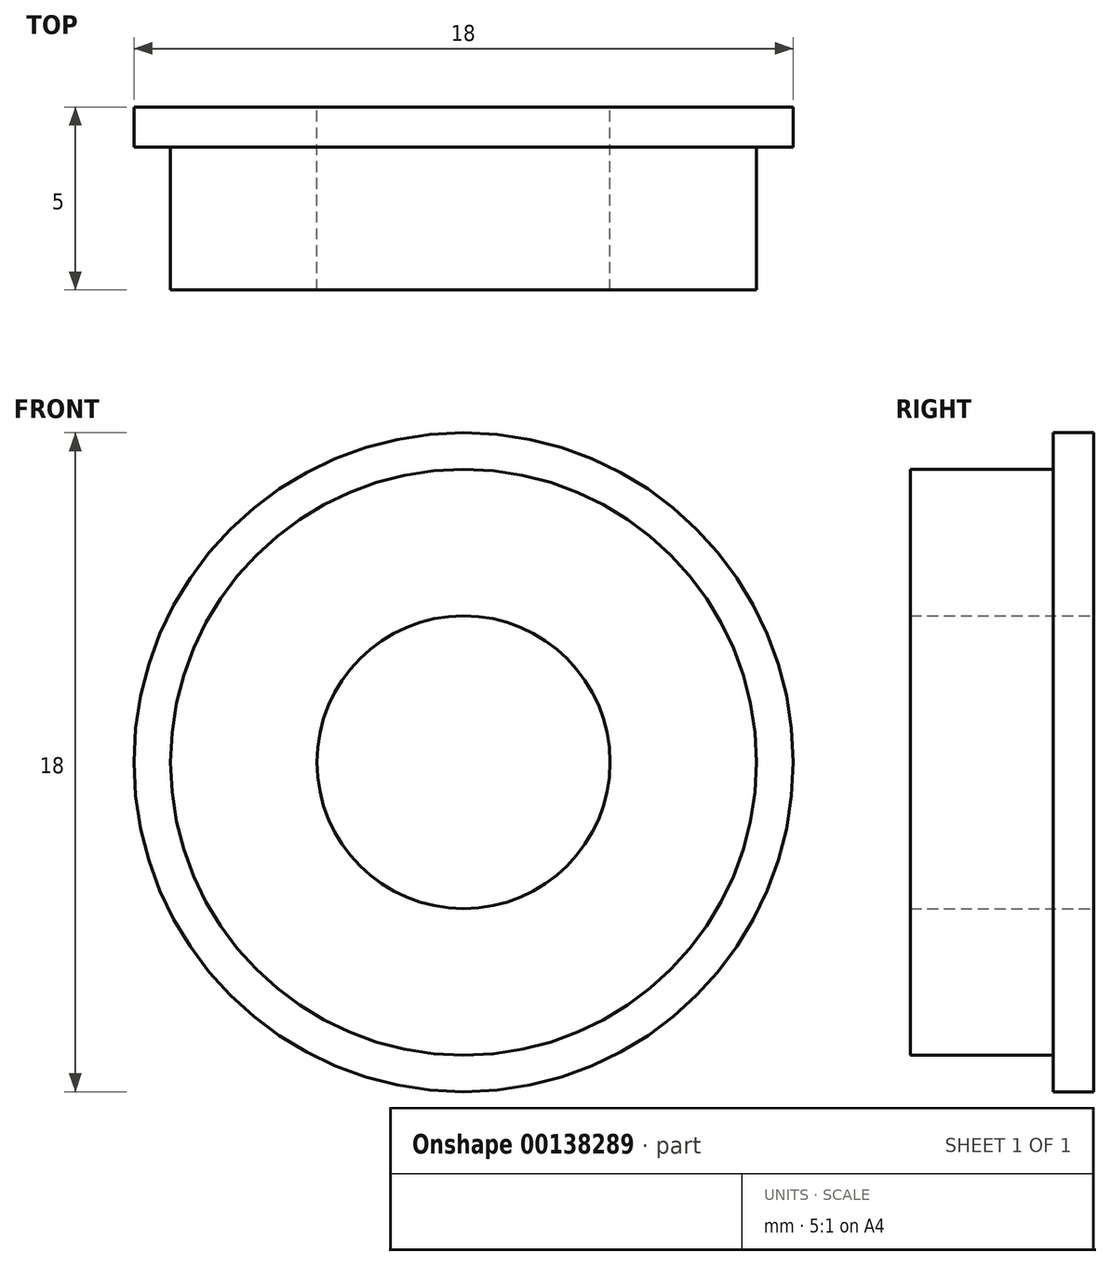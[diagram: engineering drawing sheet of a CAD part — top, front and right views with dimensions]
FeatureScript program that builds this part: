
annotation { "Feature Type Name" : "Feature", "Feature Type Description" : "" }
export const myFeature = defineFeature(function(context is Context, id is Id, definition is map)
    precondition{}
    {
        {
            var Q0;
            Q0=qCreatedBy(makeId("Front.planeOp"),FACE);
            var sketch = newSketch(context, id + "F0", { "sketchPlane" : qUnion([Q0])});
            skCircle(sketch, "E0", {"center": v(0, 0) * mm, "radius": 8 * mm});
            skCircle(sketch, "E1", {"center": v(0, 0) * mm, "radius": 4 * mm});
            skSolve(sketch);
        }
        {
            var Q0;
            Q0=makeQuery(id+"F0.imprint","IMPRINT",FACE,{"disambiguationData":[TD([[makeQuery(id+"F0.imprint","IMPRINT",EDGE,{"derivedFrom":sQuery(id+"F0.wireOp",EDGE,"E0")}),1.0]])]});
            extrude(context, id + "F1", {"entities" : qUnion([Q0]), "depth" : 5 * mm});
        }
        {
            var Q0;
            Q0=makeQuery(id+"F1.opExtrude","CAP_FACE",FACE,{"disambiguationData":[OSD([sQuery(id+"F0.wireOp",EDGE,"E0"),sQuery(id+"F0.wireOp",EDGE,"E1")])],"isStart":true});
            var sketch = newSketch(context, id + "F2", { "sketchPlane" : qUnion([Q0])});
            skCircle(sketch, "E2", {"center": v(0, 0) * mm, "radius": 9 * mm});
            skCircle(sketch, "E3.0", {"center": v(0, 0) * mm, "radius": 8 * mm});
            skSolve(sketch);
        }
        {
            var Q0;
            Q0=makeQuery(id+"F2.imprint","IMPRINT",FACE,{"disambiguationData":[TD([[makeQuery(id+"F2.imprint","IMPRINT",EDGE,{"derivedFrom":sQuery(id+"F2.wireOp",EDGE,"E2")}),1.0]])]});
            extrude(context, id + "F3", {"entities" : qUnion([Q0]), "operationType" : NewBodyOperationType.ADD, "oppositeDirection" : true, "depth" : 1.1 * mm});
        }
    });
